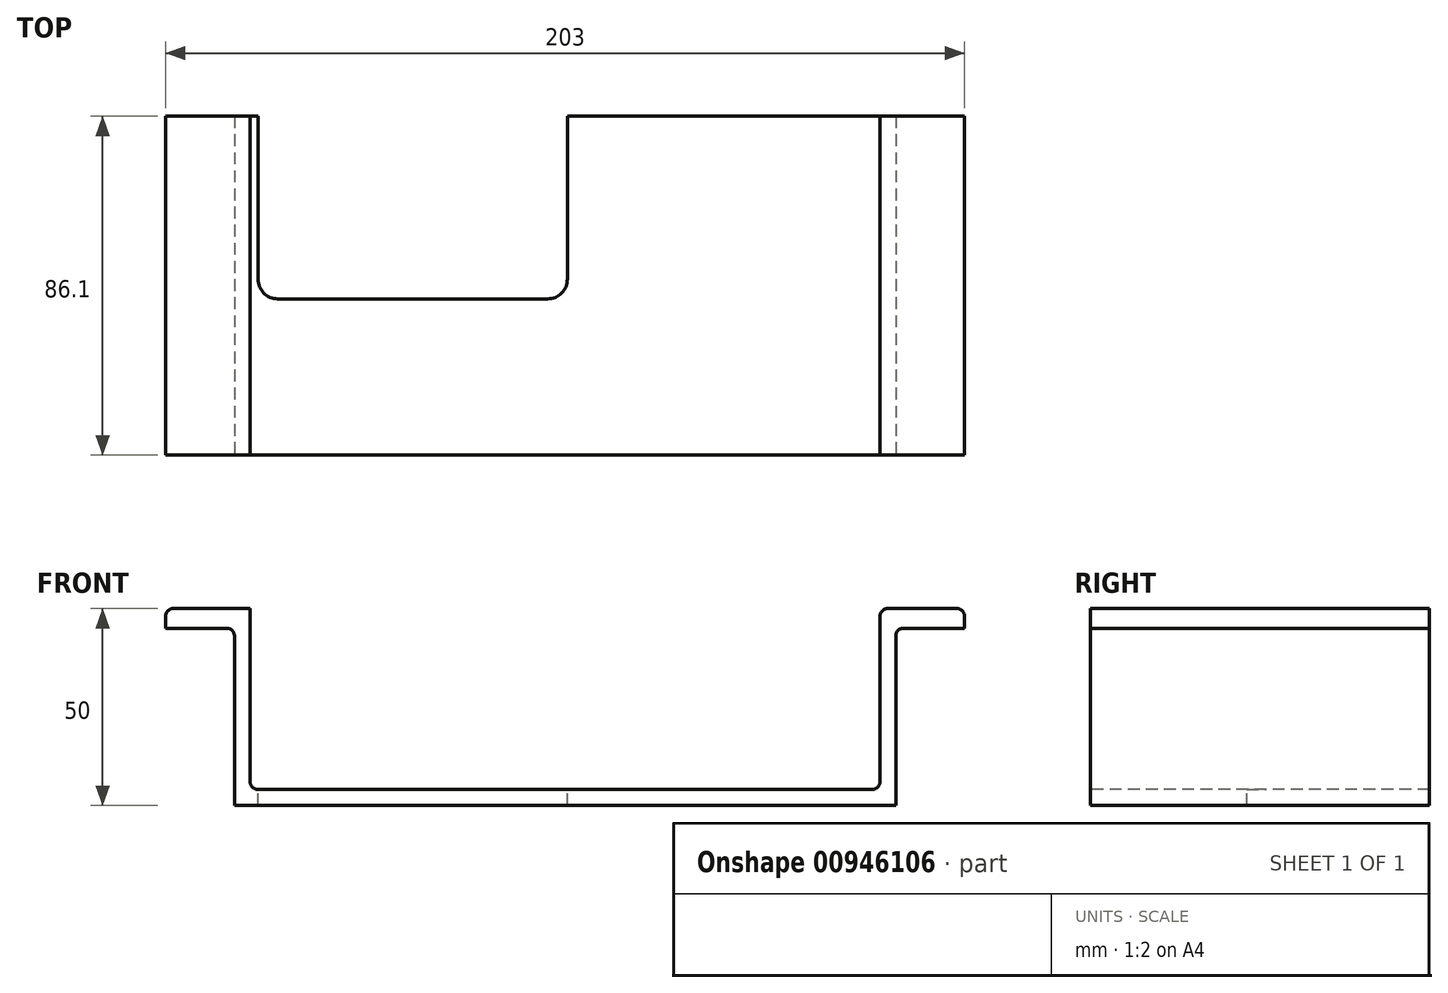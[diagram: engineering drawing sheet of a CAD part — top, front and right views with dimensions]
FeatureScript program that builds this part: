
annotation { "Feature Type Name" : "Feature", "Feature Type Description" : "" }
export const myFeature = defineFeature(function(context is Context, id is Id, definition is map)
    precondition{}
    {
        {
            var Q0;
            Q0=qCreatedBy(makeId("Top.planeOp"),FACE);
            var sketch = newSketch(context, id + "F0", { "sketchPlane" : qUnion([Q0])});
            skLineSegment(sketch, "E0.bottom", {"start": v(-102.08, 41.03) * mm, "end": v(100.92, 41.03) * mm});
            skLineSegment(sketch, "E0.top", {"start": v(-102.08, -45.07) * mm, "end": v(100.92, -45.07) * mm});
            skLineSegment(sketch, "E0.left", {"start": v(-102.08, 41.03) * mm, "end": v(-102.08, -45.07) * mm});
            skLineSegment(sketch, "E0.right", {"start": v(100.92, 41.03) * mm, "end": v(100.92, -45.07) * mm});
            skSolve(sketch);
        }
        {
            var Q0;
            Q0 = qSketchRegion(id + "F0", true);
            extrude(context, id + "F1", {"entities" : qUnion([Q0]), "depth" : 50 * mm, "offsetDistance" : 25 * mm});
        }
        {
            var Q0;
            Q0=makeQuery(id+"F1.opExtrude","SWEPT_FACE",FACE,{"disambiguationData":[OSD([sQuery(id+"F0.wireOp",EDGE,"E0.top")])]});
            var sketch = newSketch(context, id + "F2", { "sketchPlane" : qUnion([Q0])});
            skLineSegment(sketch, "E1.bottom", {"start": v(-102.08, 0) * mm, "end": v(-84.58, 0) * mm});
            skLineSegment(sketch, "E1.top", {"start": v(-102.08, 45) * mm, "end": v(-84.58, 45) * mm});
            skLineSegment(sketch, "E1.left", {"start": v(-102.08, 0) * mm, "end": v(-102.08, 45) * mm});
            skLineSegment(sketch, "E1.right", {"start": v(-84.58, 0) * mm, "end": v(-84.58, 45) * mm});
            skSolve(sketch);
        }
        {
            var Q0;
            Q0 = qSketchRegion(id + "F2", true);
            extrude(context, id + "F3", {"entities" : qUnion([Q0]), "operationType" : NewBodyOperationType.REMOVE, "endBound" : BoundingType.THROUGH_ALL, "oppositeDirection" : true, "depth" : 25 * mm, "offsetDistance" : 25 * mm});
        }
        {
            var Q0;
            Q0=makeQuery(id+"F1.opExtrude","SWEPT_FACE",FACE,{"disambiguationData":[OSD([sQuery(id+"F0.wireOp",EDGE,"E0.top")])]});
            var sketch = newSketch(context, id + "F4", { "sketchPlane" : qUnion([Q0])});
            skLineSegment(sketch, "E2.bottom", {"start": v(100.92, 0) * mm, "end": v(83.42, 0) * mm});
            skLineSegment(sketch, "E2.top", {"start": v(100.92, 45) * mm, "end": v(83.42, 45) * mm});
            skLineSegment(sketch, "E2.left", {"start": v(100.92, 0) * mm, "end": v(100.92, 45) * mm});
            skLineSegment(sketch, "E2.right", {"start": v(83.42, 0) * mm, "end": v(83.42, 45) * mm});
            skSolve(sketch);
        }
        {
            var Q0;
            Q0 = qSketchRegion(id + "F4", true);
            extrude(context, id + "F5", {"entities" : qUnion([Q0]), "operationType" : NewBodyOperationType.REMOVE, "endBound" : BoundingType.THROUGH_ALL, "oppositeDirection" : true, "depth" : 25 * mm, "offsetDistance" : 25 * mm});
        }
        {
            var Q0;
            Q0=makeQuery(id+"F1.opExtrude","SWEPT_FACE",FACE,{"disambiguationData":[OSD([sQuery(id+"F0.wireOp",EDGE,"E0.top")])]});
            var sketch = newSketch(context, id + "F6", { "sketchPlane" : qUnion([Q0])});
            skLineSegment(sketch, "E3.bottom", {"start": v(-80.58, 50) * mm, "end": v(79.42, 50) * mm});
            skLineSegment(sketch, "E3.top", {"start": v(-80.58, 4) * mm, "end": v(79.42, 4) * mm});
            skLineSegment(sketch, "E3.left", {"start": v(-80.58, 50) * mm, "end": v(-80.58, 4) * mm});
            skLineSegment(sketch, "E3.right", {"start": v(79.42, 50) * mm, "end": v(79.42, 4) * mm});
            skSolve(sketch);
        }
        {
            var Q0;
            Q0 = qSketchRegion(id + "F6", true);
            extrude(context, id + "F7", {"entities" : qUnion([Q0]), "operationType" : NewBodyOperationType.REMOVE, "endBound" : BoundingType.THROUGH_ALL, "oppositeDirection" : true, "depth" : 25 * mm, "offsetDistance" : 25 * mm});
        }
        {
            var Q0;
            Q0=makeQuery(id+"F7.boolean.opBoolean","COPY",EDGE,{"derivedFrom":makeQuery(id+"F7.opExtrude","SWEPT_EDGE",EDGE,{"disambiguationData":[OSD([sQuery(id+"F0.wireOp",EDGE,"E0.top"),sQuery(id+"F6.wireOp",EDGE,"E3.bottom"),sQuery(id+"F6.wireOp",EDGE,"E3.right")])]})});
            var Q1;
            Q1=makeQuery(id+"F7.boolean.opBoolean","COPY",EDGE,{"derivedFrom":makeQuery(id+"F7.opExtrude","SWEPT_EDGE",EDGE,{"disambiguationData":[OSD([sQuery(id+"F0.wireOp",EDGE,"E0.top"),sQuery(id+"F6.wireOp",EDGE,"E3.bottom"),sQuery(id+"F6.wireOp",EDGE,"E3.left")])]})});
            var Q2;
            Q2=makeQuery(id+"F3.boolean.opBoolean","COPY",EDGE,{"derivedFrom":makeQuery(id+"F3.opExtrude","SWEPT_EDGE",EDGE,{"disambiguationData":[OSD([sQuery(id+"F2.wireOp",EDGE,"E1.top"),sQuery(id+"F2.wireOp",EDGE,"E1.right")])]})});
            var Q3;
            Q3=makeQuery(id+"F5.boolean.opBoolean","COPY",EDGE,{"derivedFrom":makeQuery(id+"F5.opExtrude","SWEPT_EDGE",EDGE,{"disambiguationData":[OSD([sQuery(id+"F4.wireOp",EDGE,"E2.top"),sQuery(id+"F4.wireOp",EDGE,"E2.right")])]})});
            var Q4;
            Q4=makeQuery(id+"F7.boolean.opBoolean","COPY",EDGE,{"derivedFrom":makeQuery(id+"F7.opExtrude","SWEPT_EDGE",EDGE,{"disambiguationData":[OSD([sQuery(id+"F6.wireOp",EDGE,"E3.top"),sQuery(id+"F6.wireOp",EDGE,"E3.right")])]})});
            var Q5;
            Q5=makeQuery(id+"F7.boolean.opBoolean","COPY",EDGE,{"derivedFrom":makeQuery(id+"F7.opExtrude","SWEPT_EDGE",EDGE,{"disambiguationData":[OSD([sQuery(id+"F6.wireOp",EDGE,"E3.top"),sQuery(id+"F6.wireOp",EDGE,"E3.left")])]})});
            var Q6;
            Q6=makeQuery(id+"F1.opExtrude","CAP_EDGE",EDGE,{"disambiguationData":[OSD([sQuery(id+"F0.wireOp",EDGE,"E0.right")])],"isStart":false});
            var Q7;
            Q7=makeQuery(id+"F1.opExtrude","CAP_EDGE",EDGE,{"disambiguationData":[OSD([sQuery(id+"F0.wireOp",EDGE,"E0.left")])],"isStart":false});
            fillet(context, id + "F8", {"entities" : qUnion([Q0, Q1, Q2, Q3, Q4, Q5, Q6, Q7]), "radius" : 2 * mm, "tangentPropagation" : true, "allowEdgeOverflow" : false});
        }
        {
            var Q0;
            Q0=makeQuery(id+"F7.boolean.opBoolean","COPY",FACE,{"derivedFrom":makeQuery(id+"F7.opExtrude","SWEPT_FACE",FACE,{"disambiguationData":[OSD([sQuery(id+"F6.wireOp",EDGE,"E3.top")])]})});
            var sketch = newSketch(context, id + "F9", { "sketchPlane" : qUnion([Q0])});
            skLineSegment(sketch, "E4.bottom", {"start": v(-78.58, 41.03) * mm, "end": v(0, 41.03) * mm});
            skLineSegment(sketch, "E4.top", {"start": v(-78.58, -5.38) * mm, "end": v(0, -5.38) * mm});
            skLineSegment(sketch, "E4.left", {"start": v(-78.58, 41.03) * mm, "end": v(-78.58, -5.38) * mm});
            skLineSegment(sketch, "E4.right", {"start": v(0, 41.03) * mm, "end": v(0, -5.38) * mm});
            skSolve(sketch);
        }
        {
            var Q0;
            Q0 = qSketchRegion(id + "F9", true);
            extrude(context, id + "F10", {"entities" : qUnion([Q0]), "operationType" : NewBodyOperationType.REMOVE, "oppositeDirection" : true, "depth" : 25 * mm, "offsetDistance" : 25 * mm});
        }
        {
            var Q0;
            Q0=makeQuery(id+"F10.boolean.opBoolean","COPY",EDGE,{"derivedFrom":makeQuery(id+"F10.opExtrude","SWEPT_EDGE",EDGE,{"disambiguationData":[OSD([sQuery(id+"F9.wireOp",EDGE,"E4.top"),sQuery(id+"F9.wireOp",EDGE,"E4.right")])]})});
            var Q1;
            Q1=makeQuery(id+"F10.boolean.opBoolean","COPY",EDGE,{"derivedFrom":makeQuery(id+"F10.opExtrude","SWEPT_EDGE",EDGE,{"disambiguationData":[OSD([sQuery(id+"F6.wireOp",EDGE,"E3.top"),sQuery(id+"F6.wireOp",EDGE,"E3.left"),sQuery(id+"F9.wireOp",EDGE,"E4.top"),sQuery(id+"F9.wireOp",EDGE,"E4.left")])]})});
            fillet(context, id + "F11", {"entities" : qUnion([Q0, Q1]), "radius" : 5 * mm, "tangentPropagation" : true, "allowEdgeOverflow" : false});
        }
    });
